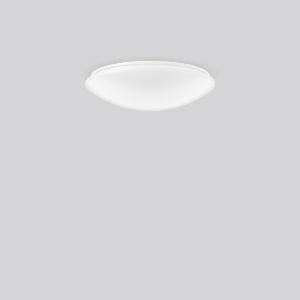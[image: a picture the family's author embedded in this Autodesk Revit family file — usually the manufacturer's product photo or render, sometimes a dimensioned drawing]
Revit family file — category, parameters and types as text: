
# Revit family: flat_polymero_672479_002_1_04_3a8f
name_source: partatom
category: Lighting Fixtures
units: mm (PartAtom-declared; Revit-internal decimal feet)

## family parameters
Cut with Voids When Loaded = No
Host = Face
Light Source = No
Part Type = Normal
Room Calculation Point = No
Round Connector Dimension = Use Diameter
Shared = No

## types (1)
- FLAT POLYMERO (1 x LED Modul 830, 1100 lm, 3000)
    Apparent Load = 13 VA
    CIE Flux Codes = 43 73 91 89 100
    Color Rendering = 80
    Color Temperature = 3000
    Default Elevation = 1800 mm
    Description = Series: FLAT POLYMERO
Decorative round surface-mounted luminaire. For escape route illumination. Base: metal, powder-coated. Diffuser made of non-yellowing plastic (PMMA), opal. Diffuser fastening: patented push system. Suitable for Ceiling mounting, Wall (surface). Self-contained system with automatic self-test and feedback to the RZB monitoring system MULTIDIGIT. 
Colour: white
Diameter: 360 mm
Height: 100 mm
Weight: 1.45 kg
Operating mode: Combined NL readiness
Duration time: 3 h
Lamp: LED
Socket: without socket
Colour temperature: 3000K
Colour rendering index (CRI): 80
System power: 13 W
Rated luminous flux: 1100 lm
Luminous flux, emergency: 150 lm
System power, emergency: -
Control gear: Converter not necessary
Protection class: I
Type of protection: IP 40
    Height = 100 mm  [stored 0.328084 ft]
    Lamp = 1 x LED Modul 830
    Lamp Light Flux = 1100 lm
    Lamp count = 1
    Length = 360 mm
    Lifetime = 50000 h
    Luminous efficacy = 85 lm/W
    Manufacturer = RZB
    ModVariant = No
    Model = 672479.002.1.04
    Mounting Place = Ceiling, Wall
    Mounting Type = Surface mounted
    Number of Poles = 1
    OnlyDefault = Yes
    Power Factor = 1
    Product Name = FLAT POLYMERO
    Product group = Surface mounted ceiling and wall luminaires
    ProductGroupID = 305
    Protection Class = Protection class I
    Protection Degree = IP 40
    RLX_Detail_Level = 1
    RLX_Emergency_Light_Flux = 0 lm
    RLX_Emergency_Type = 0
    RLX_Emergency_Type_DB = No
    RlxData = <blob elided: 76345 chars, md5=62b2dd6c>
    Socket = socket
    Standby Power = 0 W
    System Light Flux = 1100 lm
    System Power = 13 W
    Type Comments = ALEA SPOT
    Type Image = 311523.002.1.jpg
    URL = http://relux.com
    VarID = ---
    Voltage = 230 V
    Voltage Range = 220-240 V
    Weight = 0.00 kg
    Width = 0 mm  [stored 0 ft]

note: [stored X ft] marks values corroborated as IEEE doubles in the binary element streams (Revit-internal decimal feet)

## geometry (parser evidence)
native form markers: Blend x4, Sweep x13
no freeform markers — native parametric forms only
